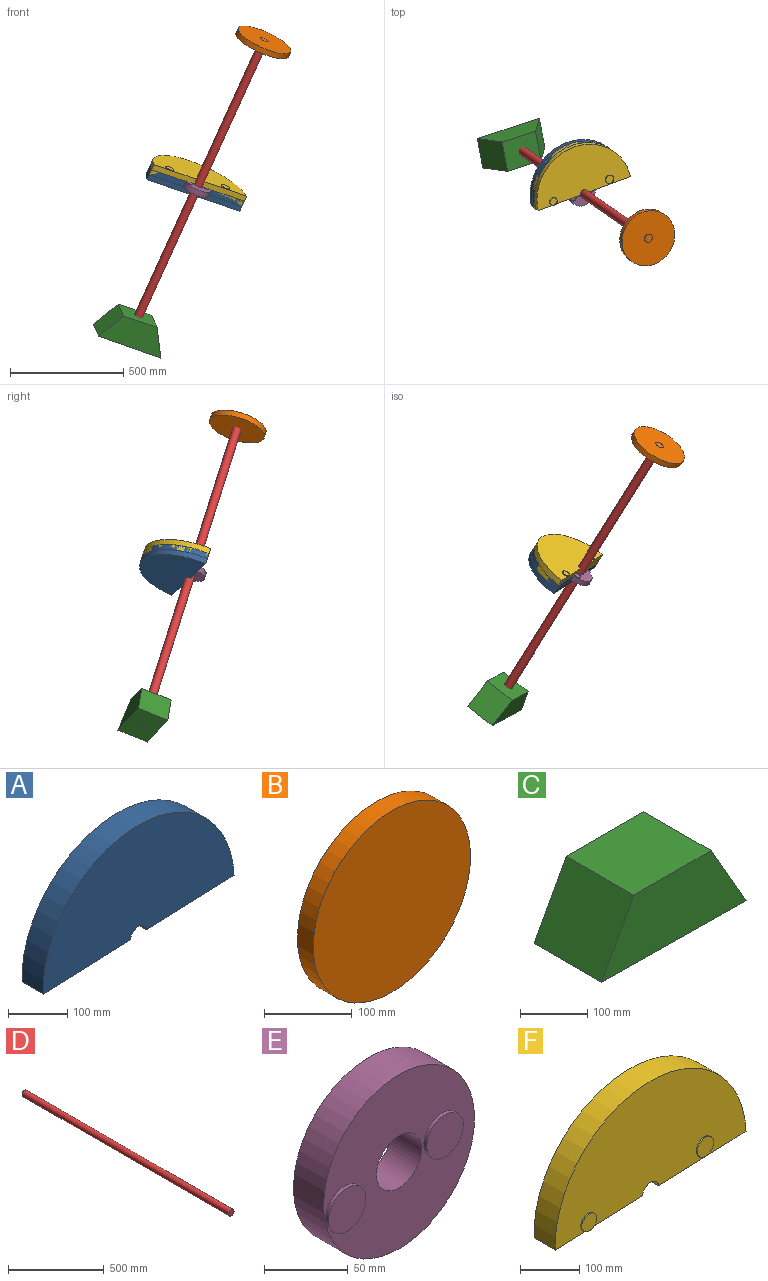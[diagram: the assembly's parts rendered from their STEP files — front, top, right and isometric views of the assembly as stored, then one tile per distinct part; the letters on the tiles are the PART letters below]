
ASSEMBLY  parts=6 mates=5
PART A: 6 faces, bbox 457x50.8x236.4 mm
  f0: plane 209.42x50.8mm, normal (0.04,0,-1), area 10646.6mm2, adj f1,f3,f4,f5
  f1: cylinder r=228.6mm len=456.98mm, axis (0,1,0), area 36371.6mm2, adj f0,f2,f4,f5
  f2: plane 209.42x50.8mm, normal (0.04,0,-1), area 10646.6mm2, adj f1,f3,f4,f5
  f3: cylinder r=19.05mm len=50.8mm, axis (0,1,0), area 2928.9mm2, adj f0,f2,f4,f5
  f4: plane 456.98x236.41mm, normal (0,-1,0), area 81057.4mm2, adj f0,f1,f2,f3
  f5: plane 456.98x236.41mm, normal (0,1,0), area 81057.4mm2, adj f0,f1,f2,f3
PART B: 3 faces, bbox 254x25.4x254 mm
  f0: cylinder r=127mm len=254mm, axis (0,1,0), area 20268.3mm2, adj f1,f2
  f1: plane 254x254mm, normal (0,-1,0), area 50670.7mm2, adj f0
  f2: plane 254x254mm, normal (0,1,0), area 50670.7mm2, adj f0
PART C: 6 faces, bbox 304.8x142.1x128.9 mm
  f0: plane 163.03x142.14mm, normal (0,0,1), area 23172.7mm2, adj f1,f3,f4,f5
  f1: plane 142.14x125.05mm, normal (-0.88,0,0.48), area 20238.2mm2, adj f0,f2,f4,f5
  f2: plane 304.78x142.14mm, normal (-0.01,0,-1), area 43322.7mm2, adj f1,f3,f4,f5
  f3: plane 142.14x128.87mm, normal (0.87,0,0.5), area 21096.7mm2, adj f0,f2,f4,f5
  f4: plane 304.78x128.87mm, normal (0,-1,0), area 29690.7mm2, adj f0,f1,f2,f3
  f5: plane 304.78x128.87mm, normal (0,1,0), area 29690.7mm2, adj f0,f1,f2,f3
PART D: 3 faces, bbox 38.1x1524x38.1 mm
  f0: cylinder r=19.05mm len=1524mm, axis (0,1,0), area 182414.7mm2, adj f1,f2
  f1: plane 38.1x38.1mm, normal (0,-1,0), area 1140.1mm2, adj f0
  f2: plane 38.1x38.1mm, normal (0,1,0), area 1140.1mm2, adj f0
PART E: 12 faces, bbox 127x30.5x127 mm
  f0: cylinder r=19.05mm len=38.1mm, axis (0,1,0), area 3040.2mm2, adj f2,f3
  f1: cylinder r=63.5mm len=127mm, axis (0,1,0), area 10134.1mm2, adj f2,f3
  f2: plane 127x127mm, normal (0,-1,0), area 10008.3mm2, adj f0,f1,f8,f10
  f3: plane 127x127mm, normal (0,1,0), area 9265mm2, adj f0,f1,f4,f6
  f4: cylinder r=18.41mm len=36.83mm, axis (0,-1,0), area 293.9mm2, adj f3,f5
  f5: plane 36.83x36.83mm, normal (0,1,0), area 1065.1mm2, adj f4
  f6: cylinder r=19.52mm len=39.05mm, axis (0,-1,0), area 311.6mm2, adj f3,f7
  f7: plane 39.05x39.05mm, normal (0,1,0), area 1197.5mm2, adj f6
  f8: cylinder r=15.75mm len=31.5mm, axis (0,1,0), area 251.4mm2, adj f2,f9
  f9: plane 31.5x31.5mm, normal (0,-1,0), area 779.5mm2, adj f8
  f10: cylinder r=15.35mm len=30.69mm, axis (0,1,0), area 244.9mm2, adj f2,f11
  f11: plane 30.69x30.69mm, normal (0,-1,0), area 739.8mm2, adj f10
PART F: 11 faces, bbox 457x53.3x236.4 mm
  f0: plane 209.42x50.8mm, normal (0.04,0,-1), area 10646.6mm2, adj f1,f3,f4,f5
  f1: cylinder r=228.6mm len=456.98mm, axis (0,1,0), area 36371.6mm2, adj f0,f2,f4,f5
  f2: plane 209.42x50.8mm, normal (0.04,0,-1), area 10646.6mm2, adj f1,f3,f4,f5,f6
  f3: cylinder r=19.05mm len=50.8mm, axis (0,1,0), area 2928.9mm2, adj f0,f2,f4,f5
  f4: plane 456.98x236.41mm, normal (0,-1,0), area 78883.4mm2, adj f0,f1,f2,f3,f7,f9
  f5: plane 456.98x236.41mm, normal (0,1,0), area 81057.4mm2, adj f0,f1,f2,f3
  f6: plane 13.42x1.6mm, normal (0,1,0), area 12mm2, adj f2,f7
  f7: cylinder r=17.68mm len=35.37mm, axis (0,1,0), area 282.2mm2, adj f4,f6,f8
  f8: plane 35.37x35.37mm, normal (0,-1,0), area 982.4mm2, adj f7
  f9: cylinder r=19.57mm len=39.15mm, axis (0,1,0), area 312.4mm2, adj f4,f10
  f10: plane 39.15x39.15mm, normal (0,-1,0), area 1203.5mm2, adj f9
PLACE A rot(axis=(-0.93,0.08,0.36),74.1deg) t=(-1328.13,337.51,-1344)mm
PLACE B rot(axis=(-0.93,0.08,0.36),74.1deg) t=(-990.59,171.33,-678.94)mm
PLACE C rot(axis=(0.61,0.66,0.44),31.9deg) t=(-1622.3,598.57,-1898.75)mm
PLACE D rot(axis=(-0.93,0.08,0.36),74.1deg) t=(-1591.39,532.58,-2004.7)mm
PLACE E rot(axis=(-0.93,0.08,0.36),74.1deg) t=(-1313.11,324.35,-1325.97)mm
PLACE F rot(axis=(-0.93,0.08,0.36),74.1deg) t=(-1318,330.45,-1321.8)mm
MATE fastened D.f0 <-> B.f0  axis (0.4,-0.28,0.87) through (-1028.3,127.25,-646.69)mm
MATE cylindrical E.f0 <-> D.f0  axis (-0.4,0.28,-0.87) through (-1332.09,338.87,-1312.71)mm
MATE revolute A.f1 <-> E.f0  axis (-0.4,0.28,-0.87) through (-1332.09,338.87,-1312.71)mm
MATE cylindrical F.f1 <-> E.f0  axis (-0.4,0.28,-0.87) through (-1321.96,331.82,-1290.5)mm
MATE fastened C.f2 <-> D.f0  axis (-0.4,0.28,-0.87) through (-1635.87,550.5,-1978.72)mm
